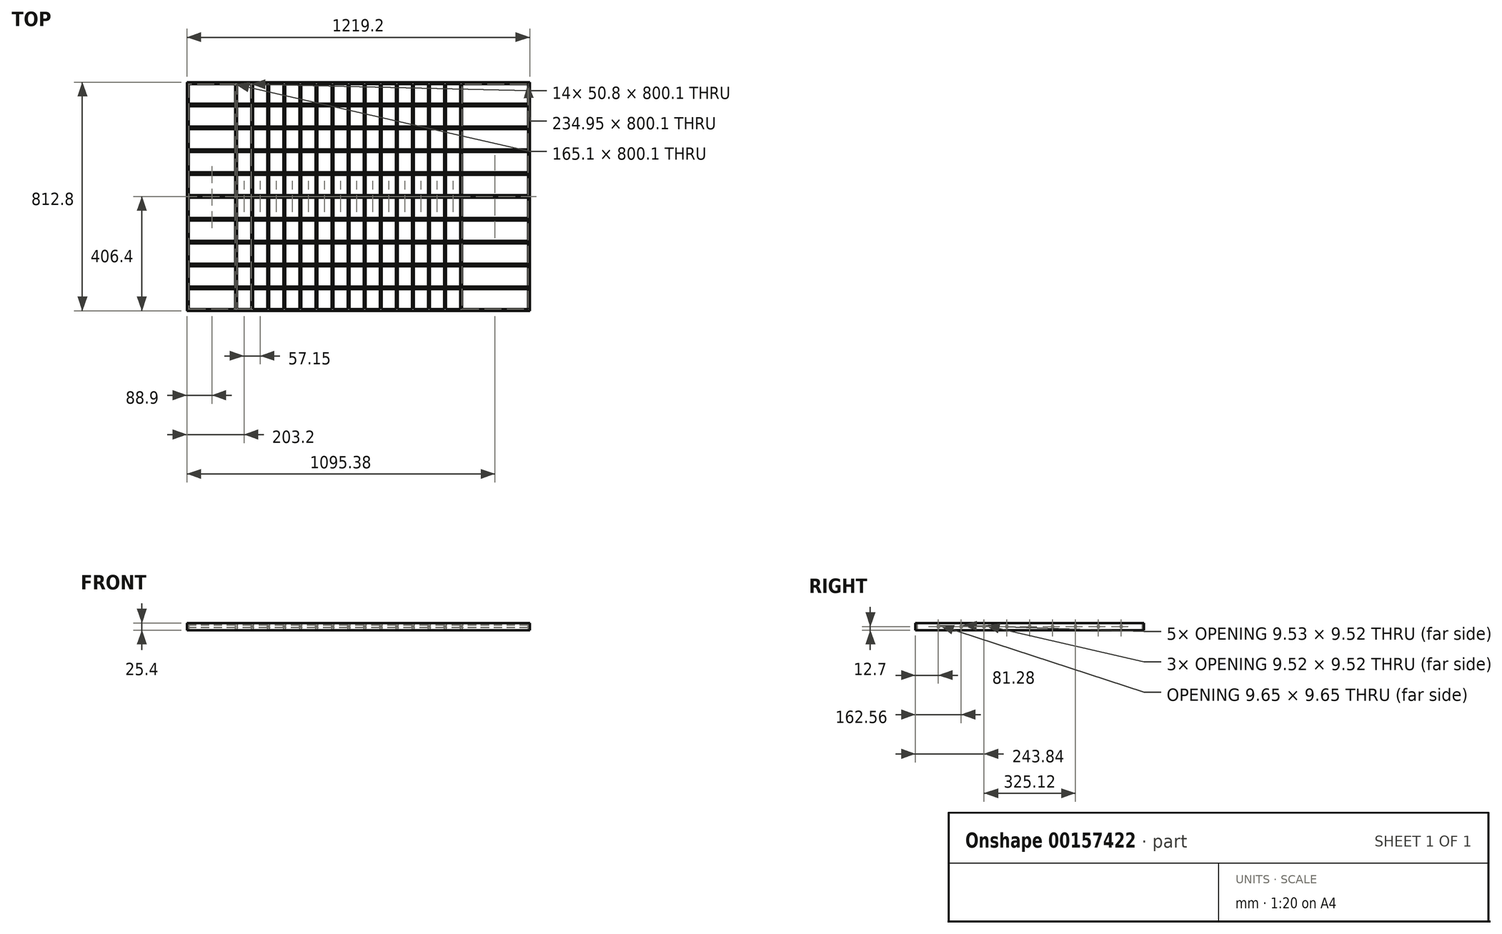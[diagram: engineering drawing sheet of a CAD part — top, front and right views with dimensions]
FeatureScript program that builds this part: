
annotation { "Feature Type Name" : "Feature", "Feature Type Description" : "" }
export const myFeature = defineFeature(function(context is Context, id is Id, definition is map)
    precondition{}
    {
        {
            var Q0;
            Q0=qCreatedBy(makeId("Top.planeOp"),FACE);
            var sketch = newSketch(context, id + "F0", { "sketchPlane" : qUnion([Q0])});
            skLineSegment(sketch, "E0.bottom", {"start": v(609.6, 406.4) * mm, "end": v(-609.6, 406.4) * mm});
            skLineSegment(sketch, "E0.top", {"start": v(609.6, -406.4) * mm, "end": v(-609.6, -406.4) * mm});
            skLineSegment(sketch, "E0.left", {"start": v(609.6, 406.4) * mm, "end": v(609.6, -406.4) * mm});
            skLineSegment(sketch, "E0.right", {"start": v(-609.6, 406.4) * mm, "end": v(-609.6, -406.4) * mm});
            skPoint(sketch, "E0.middle", {"position": v(0, 0) * mm});
            skLineSegment(sketch, "E1.bottom", {"start": v(603.25, 400.05) * mm, "end": v(-603.25, 400.05) * mm});
            skLineSegment(sketch, "E1.top", {"start": v(603.25, -400.05) * mm, "end": v(-603.25, -400.05) * mm});
            skLineSegment(sketch, "E1.left", {"start": v(603.25, 400.05) * mm, "end": v(603.25, -400.05) * mm});
            skLineSegment(sketch, "E1.right", {"start": v(-603.25, 400.05) * mm, "end": v(-603.25, -400.05) * mm});
            skLineSegment(sketch, "E2.bottom", {"start": v(-552.45, 400.05) * mm, "end": v(740.52, 400.05) * mm});
            skLineSegment(sketch, "E2.top", {"start": v(-546.1, -400.05) * mm, "end": v(476.25, -400.05) * mm});
            skLineSegment(sketch, "E3.bottom", {"start": v(546.1, 400.05) * mm, "end": v(-546.1, 400.05) * mm});
            skLineSegment(sketch, "E3.top", {"start": v(546.1, -400.05) * mm, "end": v(539.75, -400.05) * mm});
            skLineSegment(sketch, "E4.bottom", {"start": v(-501.65, -400.05) * mm, "end": v(76.2, -400.05) * mm});
            skLineSegment(sketch, "E4.top", {"start": v(-450.85, 400.05) * mm, "end": v(501.65, 400.05) * mm});
            skLineSegment(sketch, "E5.bottom", {"start": v(-488.95, 400.05) * mm, "end": v(-450.85, 400.05) * mm});
            skLineSegment(sketch, "E5.top", {"start": v(-501.65, -400.05) * mm, "end": v(-495.3, -400.05) * mm});
            skLineSegment(sketch, "E6.bottom", {"start": v(-488.95, 400.05) * mm, "end": v(-381, 400.05) * mm});
            skLineSegment(sketch, "E6.top", {"start": v(-495.3, -400.05) * mm, "end": v(-381, -400.05) * mm});
            skLineSegment(sketch, "E6.right", {"start": v(-381, 400.05) * mm, "end": v(-381, -400.05) * mm});
            skLineSegment(sketch, "E7.bottom", {"start": v(-374.65, 400.05) * mm, "end": v(-323.85, 400.05) * mm});
            skLineSegment(sketch, "E7.top", {"start": v(-374.65, -400.05) * mm, "end": v(-323.85, -400.05) * mm});
            skLineSegment(sketch, "E7.left", {"start": v(-374.65, 400.05) * mm, "end": v(-374.65, -400.05) * mm});
            skLineSegment(sketch, "E7.right", {"start": v(-323.85, 400.05) * mm, "end": v(-323.85, -400.05) * mm});
            skLineSegment(sketch, "E8.bottom", {"start": v(-317.5, 400.05) * mm, "end": v(-266.7, 400.05) * mm});
            skLineSegment(sketch, "E8.top", {"start": v(-317.5, -406.4) * mm, "end": v(-266.7, -406.4) * mm});
            skLineSegment(sketch, "E8.left", {"start": v(-317.5, 400.05) * mm, "end": v(-317.5, -406.4) * mm});
            skLineSegment(sketch, "E8.right", {"start": v(-266.7, 400.05) * mm, "end": v(-266.7, -406.4) * mm});
            skLineSegment(sketch, "E9.bottom", {"start": v(-260.35, 400.05) * mm, "end": v(-209.55, 400.05) * mm});
            skLineSegment(sketch, "E9.top", {"start": v(-260.35, -400.05) * mm, "end": v(-209.55, -400.05) * mm});
            skLineSegment(sketch, "E9.left", {"start": v(-260.35, 400.05) * mm, "end": v(-260.35, -400.05) * mm});
            skLineSegment(sketch, "E9.right", {"start": v(-209.55, 400.05) * mm, "end": v(-209.55, -400.05) * mm});
            skLineSegment(sketch, "E10.bottom", {"start": v(-203.2, 400.05) * mm, "end": v(-152.4, 400.05) * mm});
            skLineSegment(sketch, "E10.top", {"start": v(-203.2, -400.05) * mm, "end": v(-152.4, -400.05) * mm});
            skLineSegment(sketch, "E10.left", {"start": v(-203.2, 400.05) * mm, "end": v(-203.2, -400.05) * mm});
            skLineSegment(sketch, "E10.right", {"start": v(-152.4, 400.05) * mm, "end": v(-152.4, -400.05) * mm});
            skLineSegment(sketch, "E11.bottom", {"start": v(-146.05, 400.05) * mm, "end": v(-95.25, 400.05) * mm});
            skLineSegment(sketch, "E11.top", {"start": v(-146.05, -400.05) * mm, "end": v(-95.25, -400.05) * mm});
            skLineSegment(sketch, "E11.left", {"start": v(-146.05, 400.05) * mm, "end": v(-146.05, -400.05) * mm});
            skLineSegment(sketch, "E11.right", {"start": v(-95.25, 400.05) * mm, "end": v(-95.25, -400.05) * mm});
            skLineSegment(sketch, "E12.bottom", {"start": v(-88.9, 400.05) * mm, "end": v(-38.1, 400.05) * mm});
            skLineSegment(sketch, "E12.top", {"start": v(-88.9, -400.05) * mm, "end": v(-38.1, -400.05) * mm});
            skLineSegment(sketch, "E12.left", {"start": v(-88.9, 400.05) * mm, "end": v(-88.9, -400.05) * mm});
            skLineSegment(sketch, "E12.right", {"start": v(-38.1, 400.05) * mm, "end": v(-38.1, -400.05) * mm});
            skLineSegment(sketch, "E13.bottom", {"start": v(-31.75, 400.05) * mm, "end": v(19.05, 400.05) * mm});
            skLineSegment(sketch, "E13.top", {"start": v(-31.75, -400.05) * mm, "end": v(19.05, -400.05) * mm});
            skLineSegment(sketch, "E13.left", {"start": v(-31.75, 400.05) * mm, "end": v(-31.75, -400.05) * mm});
            skLineSegment(sketch, "E13.right", {"start": v(19.05, 400.05) * mm, "end": v(19.05, -400.05) * mm});
            skLineSegment(sketch, "E14.bottom", {"start": v(25.4, 400.05) * mm, "end": v(76.2, 400.05) * mm});
            skLineSegment(sketch, "E14.top", {"start": v(25.4, -400.05) * mm, "end": v(76.2, -400.05) * mm});
            skLineSegment(sketch, "E14.left", {"start": v(25.4, 400.05) * mm, "end": v(25.4, -400.05) * mm});
            skLineSegment(sketch, "E14.right", {"start": v(76.2, 400.05) * mm, "end": v(76.2, -400.05) * mm});
            skLineSegment(sketch, "E15.bottom", {"start": v(82.55, 400.05) * mm, "end": v(133.35, 400.05) * mm});
            skLineSegment(sketch, "E15.top", {"start": v(82.55, -400.05) * mm, "end": v(133.35, -400.05) * mm});
            skLineSegment(sketch, "E15.left", {"start": v(82.55, 400.05) * mm, "end": v(82.55, -400.05) * mm});
            skLineSegment(sketch, "E15.right", {"start": v(133.35, 400.05) * mm, "end": v(133.35, -400.05) * mm});
            skLineSegment(sketch, "E16.bottom", {"start": v(139.7, 400.05) * mm, "end": v(190.5, 400.05) * mm});
            skLineSegment(sketch, "E16.top", {"start": v(139.7, -400.05) * mm, "end": v(190.5, -400.05) * mm});
            skLineSegment(sketch, "E16.left", {"start": v(139.7, 400.05) * mm, "end": v(139.7, -400.05) * mm});
            skLineSegment(sketch, "E16.right", {"start": v(190.5, 400.05) * mm, "end": v(190.5, -400.05) * mm});
            skLineSegment(sketch, "E17.bottom", {"start": v(196.85, 400.05) * mm, "end": v(247.65, 400.05) * mm});
            skLineSegment(sketch, "E17.top", {"start": v(196.85, -400.05) * mm, "end": v(247.65, -400.05) * mm});
            skLineSegment(sketch, "E17.left", {"start": v(196.85, 400.05) * mm, "end": v(196.85, -400.05) * mm});
            skLineSegment(sketch, "E17.right", {"start": v(247.65, 400.05) * mm, "end": v(247.65, -400.05) * mm});
            skLineSegment(sketch, "E18.bottom", {"start": v(254, 400.05) * mm, "end": v(304.8, 400.05) * mm});
            skLineSegment(sketch, "E18.top", {"start": v(254, -400.05) * mm, "end": v(304.8, -400.05) * mm});
            skLineSegment(sketch, "E18.left", {"start": v(254, 400.05) * mm, "end": v(254, -400.05) * mm});
            skLineSegment(sketch, "E18.right", {"start": v(304.8, 400.05) * mm, "end": v(304.8, -400.05) * mm});
            skLineSegment(sketch, "E19.bottom", {"start": v(311.15, 400.05) * mm, "end": v(361.95, 400.05) * mm});
            skLineSegment(sketch, "E19.top", {"start": v(311.15, -400.05) * mm, "end": v(361.95, -400.05) * mm});
            skLineSegment(sketch, "E19.left", {"start": v(311.15, 400.05) * mm, "end": v(311.15, -400.05) * mm});
            skLineSegment(sketch, "E19.right", {"start": v(361.95, 400.05) * mm, "end": v(361.95, -400.05) * mm});
            skLineSegment(sketch, "E20.bottom", {"start": v(368.3, 400.05) * mm, "end": v(419.1, 400.05) * mm});
            skLineSegment(sketch, "E20.top", {"start": v(368.3, -400.05) * mm, "end": v(419.1, -400.05) * mm});
            skLineSegment(sketch, "E20.left", {"start": v(368.3, 400.05) * mm, "end": v(368.3, -400.05) * mm});
            skLineSegment(sketch, "E20.right", {"start": v(419.1, 400.05) * mm, "end": v(419.1, -400.05) * mm});
            skLineSegment(sketch, "E21.bottom", {"start": v(419.1, 400.05) * mm, "end": v(425.45, 400.05) * mm});
            skLineSegment(sketch, "E21.top", {"start": v(419.1, -400.05) * mm, "end": v(425.45, -400.05) * mm});
            skLineSegment(sketch, "E21.right", {"start": v(425.45, 400.05) * mm, "end": v(425.45, -400.05) * mm});
            skLineSegment(sketch, "E22.bottom", {"start": v(425.45, 400.05) * mm, "end": v(476.25, 400.05) * mm});
            skLineSegment(sketch, "E22.top", {"start": v(425.45, -400.05) * mm, "end": v(476.25, -400.05) * mm});
            skLineSegment(sketch, "E22.right", {"start": v(476.25, 400.05) * mm, "end": v(476.25, -400.05) * mm});
            skLineSegment(sketch, "E23.bottom", {"start": v(476.25, 400.05) * mm, "end": v(482.6, 400.05) * mm});
            skLineSegment(sketch, "E23.top", {"start": v(476.25, -400.05) * mm, "end": v(482.6, -400.05) * mm});
            skLineSegment(sketch, "E23.right", {"start": v(482.6, 400.05) * mm, "end": v(482.6, -400.05) * mm});
            skLineSegment(sketch, "E24.bottom", {"start": v(482.6, 400.05) * mm, "end": v(533.4, 400.05) * mm});
            skLineSegment(sketch, "E24.top", {"start": v(482.6, -400.05) * mm, "end": v(533.4, -400.05) * mm});
            skLineSegment(sketch, "E24.right", {"start": v(533.4, 400.05) * mm, "end": v(533.4, -400.05) * mm});
            skLineSegment(sketch, "E25.bottom", {"start": v(533.4, 400.05) * mm, "end": v(539.75, 400.05) * mm});
            skLineSegment(sketch, "E25.top", {"start": v(533.4, -400.05) * mm, "end": v(539.75, -400.05) * mm});
            skLineSegment(sketch, "E25.right", {"start": v(539.75, 400.05) * mm, "end": v(539.75, -400.05) * mm});
            skLineSegment(sketch, "E26.bottom", {"start": v(539.75, 400.05) * mm, "end": v(590.55, 400.05) * mm});
            skLineSegment(sketch, "E26.top", {"start": v(539.75, 400.05) * mm, "end": v(590.55, 400.05) * mm});
            skLineSegment(sketch, "E26.left", {"start": v(539.75, 400.05) * mm, "end": v(539.75, 400.05) * mm});
            skLineSegment(sketch, "E26.right", {"start": v(590.55, 400.05) * mm, "end": v(590.55, 400.05) * mm});
            skLineSegment(sketch, "E27.bottom", {"start": v(539.75, 400.05) * mm, "end": v(618.1, 400.05) * mm});
            skLineSegment(sketch, "E27.top", {"start": v(539.75, -400.05) * mm, "end": v(567.3, -400.05) * mm});
            skLineSegment(sketch, "E28.bottom", {"start": v(590.55, 400.05) * mm, "end": v(596.9, 400.05) * mm});
            skLineSegment(sketch, "E28.top", {"start": v(590.55, -400.05) * mm, "end": v(596.9, -400.05) * mm});
            skLineSegment(sketch, "E29.bottom", {"start": v(-438.15, -400.05) * mm, "end": v(-457.2, -400.05) * mm});
            skLineSegment(sketch, "E29.top", {"start": v(-406.4, 400.05) * mm, "end": v(-438.15, 400.05) * mm});
            skLineSegment(sketch, "E29.right", {"start": v(-438.15, -400.05) * mm, "end": v(-438.15, 400.05) * mm});
            skLineSegment(sketch, "E30.bottom", {"start": v(-431.8, -400.05) * mm, "end": v(-488.95, -400.05) * mm});
            skLineSegment(sketch, "E30.top", {"start": v(-431.8, 400.05) * mm, "end": v(-488.95, 400.05) * mm});
            skLineSegment(sketch, "E30.left", {"start": v(-431.8, -400.05) * mm, "end": v(-431.8, 400.05) * mm});
            skLineSegment(sketch, "E30.right", {"start": v(-488.95, -400.05) * mm, "end": v(-488.95, 400.05) * mm});
            skLineSegment(sketch, "E31.bottom", {"start": v(-495.3, -400.05) * mm, "end": v(-546.1, -400.05) * mm});
            skLineSegment(sketch, "E31.top", {"start": v(-495.3, 400.05) * mm, "end": v(-546.1, 400.05) * mm});
            skLineSegment(sketch, "E31.left", {"start": v(-495.3, -400.05) * mm, "end": v(-495.3, 400.05) * mm});
            skLineSegment(sketch, "E31.right", {"start": v(-546.1, -400.05) * mm, "end": v(-546.1, 400.05) * mm});
            skLineSegment(sketch, "E32.bottom", {"start": v(-546.1, 400.05) * mm, "end": v(-552.45, 400.05) * mm});
            skLineSegment(sketch, "E32.left", {"start": v(-546.1, 400.05) * mm, "end": v(-546.1, -400.05) * mm});
            skLineSegment(sketch, "E32.right", {"start": v(-552.45, 400.05) * mm, "end": v(-552.45, -400.05) * mm});
            skLineSegment(sketch, "E33.trimOffspring", {"start": v(533.4, -400.05) * mm, "end": v(-546.1, -400.05) * mm});
            skLineSegment(sketch, "E34.trimOffspring", {"start": v(539.75, -400.05) * mm, "end": v(552.45, -400.05) * mm});
            skLineSegment(sketch, "E35.trimOffspring", {"start": v(425.45, -400.05) * mm, "end": v(450.85, -400.05) * mm});
            skLineSegment(sketch, "E36.trimOffspring", {"start": v(82.55, -400.05) * mm, "end": v(419.1, -400.05) * mm});
            skPoint(sketch, "E37.orphan", {"position": v(-740.52, -400.05) * mm});
            skSolve(sketch);
        }
        {
            var Q0;
            Q0=qSketchRegion(id+"F0",true);
            var Q1;
            Q1=makeQuery(id+"F0.imprint","IMPRINT",FACE,{"disambiguationData":[TD([[makeQuery(id+"F0.imprint","IMPRINT",EDGE,{"derivedFrom":sQuery(id+"F0.wireOp",EDGE,"E32.bottom")}),1.0]])]});
            var Q2;
            Q2=makeQuery(id+"F0.imprint","IMPRINT",FACE,{"disambiguationData":[TD([[makeQuery(id+"F0.imprint","IMPRINT",EDGE,{"derivedFrom":sQuery(id+"F0.wireOp",EDGE,"E3.bottom")}),1.0]])]});
            var Q3;
            {var subQ0=sQuery(id+"F0.wireOp",EDGE,"E29.right");Q3=makeQuery(id+"F0.imprint","IMPRINT",FACE,{"disambiguationData":[TD([[makeQuery(id+"F0.imprint","IMPRINT",EDGE,{"derivedFrom":subQ0}),-1.0]])]});}
            var Q4;
            {var subQ0=sQuery(id+"F0.wireOp",EDGE,"E6.right");Q4=makeQuery(id+"F0.imprint","IMPRINT",FACE,{"disambiguationData":[TD([[makeQuery(id+"F0.imprint","IMPRINT",EDGE,{"derivedFrom":subQ0}),1.0]])]});}
            var Q5;
            {var subQ0=sQuery(id+"F0.wireOp",EDGE,"E7.right");Q5=makeQuery(id+"F0.imprint","IMPRINT",FACE,{"disambiguationData":[TD([[makeQuery(id+"F0.imprint","IMPRINT",EDGE,{"derivedFrom":subQ0}),1.0]])]});}
            var Q6;
            {var subQ3=sQuery(id+"F0.wireOp",EDGE,"E9.left");Q6=makeQuery(id+"F0.imprint","IMPRINT",FACE,{"disambiguationData":[TD([[makeQuery(id+"F0.imprint","IMPRINT",EDGE,{"derivedFrom":subQ3}),-1.0]])]});}
            var Q7;
            {var subQ0=sQuery(id+"F0.wireOp",EDGE,"E9.right");Q7=makeQuery(id+"F0.imprint","IMPRINT",FACE,{"disambiguationData":[TD([[makeQuery(id+"F0.imprint","IMPRINT",EDGE,{"derivedFrom":subQ0}),1.0]])]});}
            var Q8;
            {var subQ0=sQuery(id+"F0.wireOp",EDGE,"E10.right");Q8=makeQuery(id+"F0.imprint","IMPRINT",FACE,{"disambiguationData":[TD([[makeQuery(id+"F0.imprint","IMPRINT",EDGE,{"derivedFrom":subQ0}),1.0]])]});}
            var Q9;
            {var subQ0=sQuery(id+"F0.wireOp",EDGE,"E11.right");Q9=makeQuery(id+"F0.imprint","IMPRINT",FACE,{"disambiguationData":[TD([[makeQuery(id+"F0.imprint","IMPRINT",EDGE,{"derivedFrom":subQ0}),1.0]])]});}
            var Q10;
            {var subQ0=sQuery(id+"F0.wireOp",EDGE,"E12.right");Q10=makeQuery(id+"F0.imprint","IMPRINT",FACE,{"disambiguationData":[TD([[makeQuery(id+"F0.imprint","IMPRINT",EDGE,{"derivedFrom":subQ0}),1.0]])]});}
            var Q11;
            {var subQ0=sQuery(id+"F0.wireOp",EDGE,"E13.right");Q11=makeQuery(id+"F0.imprint","IMPRINT",FACE,{"disambiguationData":[TD([[makeQuery(id+"F0.imprint","IMPRINT",EDGE,{"derivedFrom":subQ0}),1.0]])]});}
            var Q12;
            {var subQ0=sQuery(id+"F0.wireOp",EDGE,"E14.right");Q12=makeQuery(id+"F0.imprint","IMPRINT",FACE,{"disambiguationData":[TD([[makeQuery(id+"F0.imprint","IMPRINT",EDGE,{"derivedFrom":subQ0}),1.0]])]});}
            var Q13;
            {var subQ0=sQuery(id+"F0.wireOp",EDGE,"E15.right");Q13=makeQuery(id+"F0.imprint","IMPRINT",FACE,{"disambiguationData":[TD([[makeQuery(id+"F0.imprint","IMPRINT",EDGE,{"derivedFrom":subQ0}),1.0]])]});}
            var Q14;
            {var subQ0=sQuery(id+"F0.wireOp",EDGE,"E16.right");Q14=makeQuery(id+"F0.imprint","IMPRINT",FACE,{"disambiguationData":[TD([[makeQuery(id+"F0.imprint","IMPRINT",EDGE,{"derivedFrom":subQ0}),1.0]])]});}
            var Q15;
            {var subQ0=sQuery(id+"F0.wireOp",EDGE,"E17.right");Q15=makeQuery(id+"F0.imprint","IMPRINT",FACE,{"disambiguationData":[TD([[makeQuery(id+"F0.imprint","IMPRINT",EDGE,{"derivedFrom":subQ0}),1.0]])]});}
            var Q16;
            {var subQ0=sQuery(id+"F0.wireOp",EDGE,"E18.right");Q16=makeQuery(id+"F0.imprint","IMPRINT",FACE,{"disambiguationData":[TD([[makeQuery(id+"F0.imprint","IMPRINT",EDGE,{"derivedFrom":subQ0}),1.0]])]});}
            var Q17;
            {var subQ2=sQuery(id+"F0.wireOp",EDGE,"E19.right");Q17=makeQuery(id+"F0.imprint","IMPRINT",FACE,{"disambiguationData":[TD([[makeQuery(id+"F0.imprint","IMPRINT",EDGE,{"derivedFrom":subQ2}),1.0]])]});}
            var Q18;
            Q18=makeQuery(id+"F0.imprint","IMPRINT",FACE,{"disambiguationData":[TD([[makeQuery(id+"F0.imprint","IMPRINT",EDGE,{"derivedFrom":sQuery(id+"F0.wireOp",EDGE,"E21.bottom")}),-1.0]])]});
            var Q19;
            Q19=makeQuery(id+"F0.imprint","IMPRINT",FACE,{"disambiguationData":[TD([[makeQuery(id+"F0.imprint","IMPRINT",EDGE,{"derivedFrom":sQuery(id+"F0.wireOp",EDGE,"E23.bottom")}),-1.0]])]});
            var Q20;
            Q20=makeQuery(id+"F0.imprint","IMPRINT",FACE,{"disambiguationData":[TD([[makeQuery(id+"F0.imprint","IMPRINT",EDGE,{"derivedFrom":sQuery(id+"F0.wireOp",EDGE,"E25.bottom")}),-1.0]])]});
            extrude(context, id + "F1", {"entities" : qUnion([Q0, Q1, Q2, Q3, Q4, Q5, Q6, Q7, Q8, Q9, Q10, Q11, Q12, Q13, Q14, Q15, Q16, Q17, Q18, Q19, Q20]), "depth" : 25.4 * mm});
        }
        {
            var Q0;
            Q0=makeQuery(id+"F1.opExtrude","SWEPT_FACE",FACE,{"disambiguationData":[OSD([sQuery(id+"F0.wireOp",EDGE,"E0.right")])]});
            var sketch = newSketch(context, id + "F2", { "sketchPlane" : qUnion([Q0])});
            skCircle(sketch, "E38", {"center": v(325.12, 12.7) * mm, "radius": 4.83 * mm});
            skCircle(sketch, "E39", {"center": v(243.84, 12.7) * mm, "radius": 4.76 * mm});
            skCircle(sketch, "E40", {"center": v(162.56, 12.7) * mm, "radius": 4.76 * mm});
            skCircle(sketch, "E41", {"center": v(81.28, 12.7) * mm, "radius": 4.76 * mm});
            skCircle(sketch, "E42", {"center": v(0, 12.7) * mm, "radius": 4.76 * mm});
            skCircle(sketch, "E43", {"center": v(-81.28, 12.7) * mm, "radius": 4.76 * mm});
            skCircle(sketch, "E44", {"center": v(-162.56, 12.7) * mm, "radius": 4.76 * mm});
            skLineSegment(sketch, "E45", {"start": v(-162.56, 12.7) * mm, "end": v(-243.84, 12.7) * mm});
            skLineSegment(sketch, "E46", {"start": v(-243.84, 12.7) * mm, "end": v(-325.12, 12.7) * mm});
            skCircle(sketch, "E47", {"center": v(-243.84, 12.7) * mm, "radius": 4.76 * mm});
            skCircle(sketch, "E48", {"center": v(-325.12, 12.7) * mm, "radius": 4.76 * mm});
            skSolve(sketch);
        }
        {
            var Q0;
            Q0=qSketchRegion(id+"F2",true);
            extrude(context, id + "F3", {"entities" : qUnion([Q0]), "operationType" : NewBodyOperationType.ADD, "oppositeDirection" : true, "depth" : 1219.2 * mm});
        }
    });
